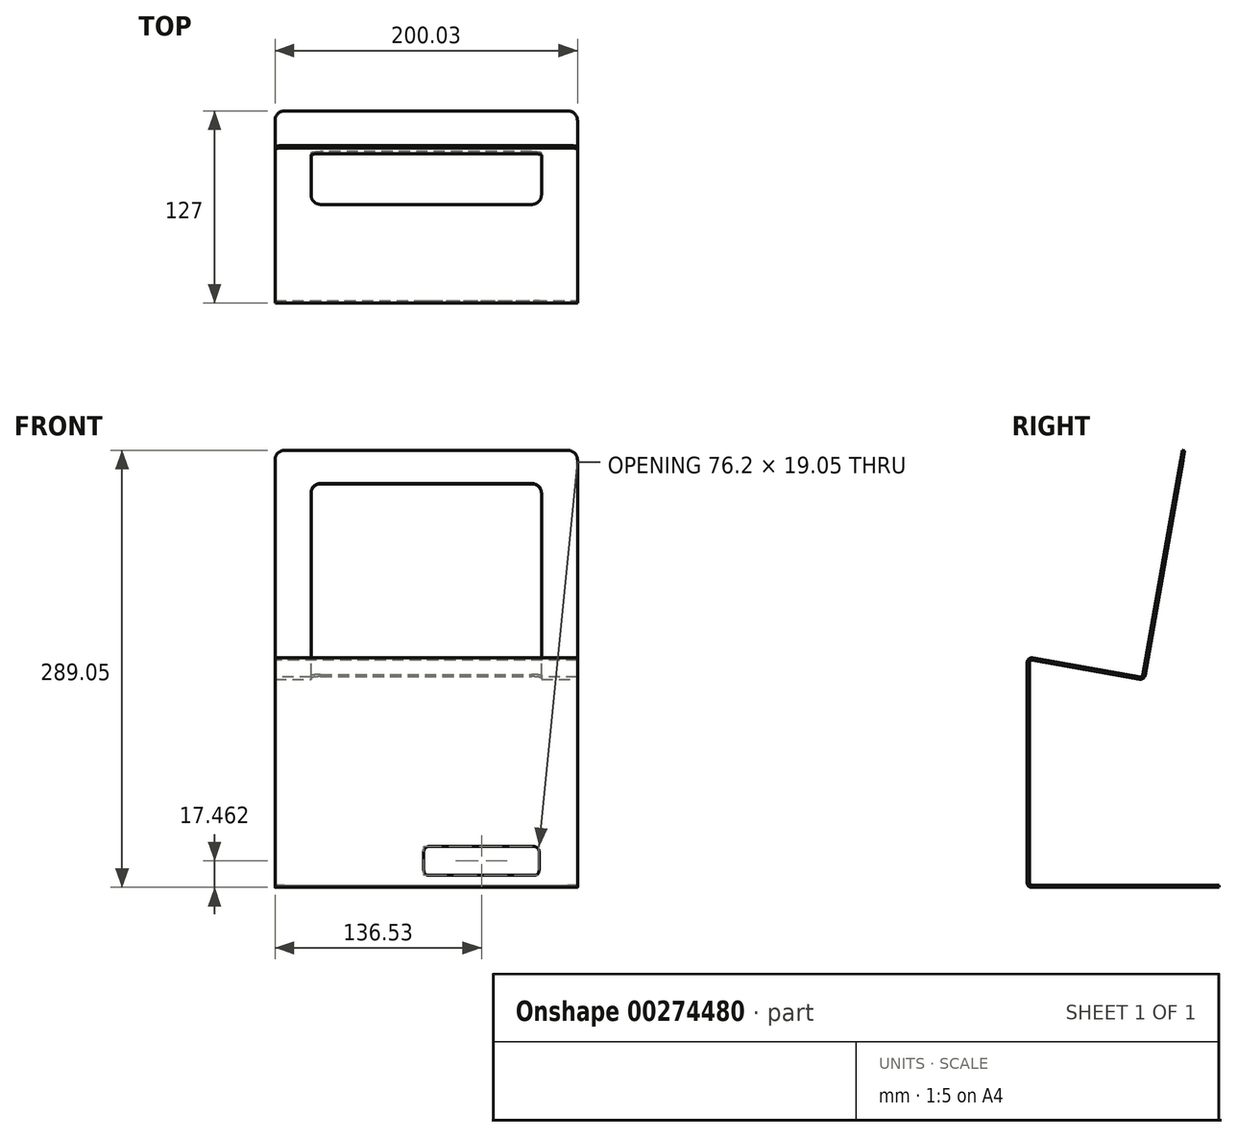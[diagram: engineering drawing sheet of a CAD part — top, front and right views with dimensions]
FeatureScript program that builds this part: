
annotation { "Feature Type Name" : "Feature", "Feature Type Description" : "" }
export const myFeature = defineFeature(function(context is Context, id is Id, definition is map)
    precondition{}
    {
        {
            var Q0;
            Q0=qCreatedBy(makeId("Right.planeOp"),FACE);
            var sketch = newSketch(context, id + "F0", { "sketchPlane" : qUnion([Q0])});
            skLineSegment(sketch, "E0", {"start": v(0, 0) * mm, "end": v(-76.2, 0) * mm});
            skLineSegment(sketch, "E1", {"start": v(-76.2, 0) * mm, "end": v(-76.2, 152.4) * mm});
            skLineSegment(sketch, "E2", {"start": v(-76.2, 152.4) * mm, "end": v(0, 138.96) * mm});
            skLineSegment(sketch, "E3", {"start": v(0, 138.96) * mm, "end": v(26.46, 289.05) * mm});
            skLineSegment(sketch, "E4.0", {"start": v(1.23, 137.2) * mm, "end": v(27.96, 288.78) * mm});
            skLineSegment(sketch, "E4.1", {"start": v(-74.68, 150.59) * mm, "end": v(1.23, 137.2) * mm});
            skLineSegment(sketch, "E4.2", {"start": v(-74.68, 1.52) * mm, "end": v(-74.68, 150.59) * mm});
            skLineSegment(sketch, "E4.3", {"start": v(0, 1.52) * mm, "end": v(-74.68, 1.52) * mm});
            skLineSegment(sketch, "E5", {"start": v(0, 1.52) * mm, "end": v(0, 0) * mm});
            skLineSegment(sketch, "E6", {"start": v(26.46, 289.05) * mm, "end": v(27.96, 288.78) * mm});
            skSolve(sketch);
        }
        {
            var Q0;
            Q0=makeQuery(id+"F0.imprint","IMPRINT",FACE,{"disambiguationData":[TD([[makeQuery(id+"F0.imprint","IMPRINT",EDGE,{"derivedFrom":sQuery(id+"F0.wireOp",EDGE,"E0")}),-1.0]])]});
            extrude(context, id + "F1", {"entities" : qUnion([Q0]), "oppositeDirection" : true, "depth" : 200.02 * mm});
        }
        {
            var Q0;
            {var subQ0=sQuery(id+"F0.wireOp",EDGE,"E3");var subQ1=sQuery(id+"F0.wireOp",EDGE,"E2");Q0=makeQuery(id+"FNieFErg1aXtviF_1.boolean.opBoolean","SPLIT",EDGE,{"disambiguationData":[TD([makeQuery(id+"FNieFErg1aXtviF_1.opExtrude","SWEPT_FACE",FACE,{"disambiguationData":[OSD([sQuery(id+"FGQBqfSR68ftS2d_1.wireOp",EDGE,"9EZzOPAj-x158-Ry3P-4ziS-DGyLsCyLf1xe.right")])]})])],"derivedFrom":makeQuery(id+"F1.opExtrude","SWEPT_EDGE",EDGE,{"disambiguationData":[OSD([subQ1,subQ0])]})});}
            var Q1;
            {var subQ0=sQuery(id+"F0.wireOp",EDGE,"E3");var subQ1=sQuery(id+"F0.wireOp",EDGE,"E2");Q1=makeQuery(id+"FNieFErg1aXtviF_1.boolean.opBoolean","SPLIT",EDGE,{"disambiguationData":[TD([makeQuery(id+"FNieFErg1aXtviF_1.opExtrude","SWEPT_FACE",FACE,{"disambiguationData":[OSD([sQuery(id+"FGQBqfSR68ftS2d_1.wireOp",EDGE,"9EZzOPAj-x158-Ry3P-4ziS-DGyLsCyLf1xe.left")])]})])],"derivedFrom":makeQuery(id+"F1.opExtrude","SWEPT_EDGE",EDGE,{"disambiguationData":[OSD([subQ1,subQ0])]})});}
            var Q2;
            Q2=makeQuery(id+"F1.opExtrude","SWEPT_EDGE",EDGE,{"disambiguationData":[OSD([sQuery(id+"F0.wireOp",EDGE,"E4.1"),sQuery(id+"F0.wireOp",EDGE,"E4.2")])]});
            var Q3;
            Q3=makeQuery(id+"F1.opExtrude","SWEPT_EDGE",EDGE,{"disambiguationData":[OSD([sQuery(id+"F0.wireOp",EDGE,"E4.2"),sQuery(id+"F0.wireOp",EDGE,"E4.3")])]});
            fillet(context, id + "F2", {"entities" : qUnion([Q0, Q1, Q2, Q3]), "radius" : 1.52 * mm, "tangentPropagation" : true, "allowEdgeOverflow" : false});
        }
        {
            var Q0;
            {var subQ0=sQuery(id+"F0.wireOp",EDGE,"E4.1");var subQ1=sQuery(id+"F0.wireOp",EDGE,"E4.0");Q0=makeQuery(id+"FNieFErg1aXtviF_1.boolean.opBoolean","SPLIT",EDGE,{"disambiguationData":[TD([makeQuery(id+"FNieFErg1aXtviF_1.opExtrude","SWEPT_FACE",FACE,{"disambiguationData":[OSD([sQuery(id+"FGQBqfSR68ftS2d_1.wireOp",EDGE,"9EZzOPAj-x158-Ry3P-4ziS-DGyLsCyLf1xe.right")])]})])],"derivedFrom":makeQuery(id+"F1.opExtrude","SWEPT_EDGE",EDGE,{"disambiguationData":[OSD([subQ1,subQ0])]})});}
            var Q1;
            {var subQ0=sQuery(id+"F0.wireOp",EDGE,"E4.1");var subQ1=sQuery(id+"F0.wireOp",EDGE,"E4.0");Q1=makeQuery(id+"FNieFErg1aXtviF_1.boolean.opBoolean","SPLIT",EDGE,{"disambiguationData":[TD([makeQuery(id+"FNieFErg1aXtviF_1.opExtrude","SWEPT_FACE",FACE,{"disambiguationData":[OSD([sQuery(id+"FGQBqfSR68ftS2d_1.wireOp",EDGE,"9EZzOPAj-x158-Ry3P-4ziS-DGyLsCyLf1xe.left")])]})])],"derivedFrom":makeQuery(id+"F1.opExtrude","SWEPT_EDGE",EDGE,{"disambiguationData":[OSD([subQ1,subQ0])]})});}
            var Q2;
            Q2=makeQuery(id+"F1.opExtrude","SWEPT_EDGE",EDGE,{"disambiguationData":[OSD([sQuery(id+"F0.wireOp",EDGE,"E1"),sQuery(id+"F0.wireOp",EDGE,"E2")])]});
            var Q3;
            Q3=makeQuery(id+"F1.opExtrude","SWEPT_EDGE",EDGE,{"disambiguationData":[OSD([sQuery(id+"F0.wireOp",EDGE,"E0"),sQuery(id+"F0.wireOp",EDGE,"E1")])]});
            fillet(context, id + "F3", {"entities" : qUnion([Q0, Q1, Q2, Q3]), "radius" : 3.04 * mm, "tangentPropagation" : true, "allowEdgeOverflow" : false});
        }
        {
            var Q0;
            Q0=makeQuery(id+"F1.opExtrude","SWEPT_FACE",FACE,{"disambiguationData":[OSD([sQuery(id+"F0.wireOp",EDGE,"E5")])]});
            extrude(context, id + "F4", {"entities" : qUnion([Q0]), "operationType" : NewBodyOperationType.ADD, "depth" : 50.8 * mm});
        }
        {
            var Q0;
            Q0=makeQuery(id+"F1.opExtrude","SWEPT_FACE",FACE,{"disambiguationData":[OSD([sQuery(id+"F0.wireOp",EDGE,"E1")])]});
            var sketch = newSketch(context, id + "F5", { "sketchPlane" : qUnion([Q0])});
            skLineSegment(sketch, "E7.bottom", {"start": v(-25.4, 7.94) * mm, "end": v(-101.6, 7.94) * mm});
            skLineSegment(sketch, "E7.top", {"start": v(-25.4, 26.99) * mm, "end": v(-101.6, 26.99) * mm});
            skLineSegment(sketch, "E7.left", {"start": v(-25.4, 7.94) * mm, "end": v(-25.4, 26.99) * mm});
            skLineSegment(sketch, "E7.right", {"start": v(-101.6, 7.94) * mm, "end": v(-101.6, 26.99) * mm});
            skSolve(sketch);
        }
        {
            var Q0;
            Q0=makeQuery(id+"F5.imprint","IMPRINT",FACE,{"disambiguationData":[TD([[makeQuery(id+"F5.imprint","IMPRINT",EDGE,{"derivedFrom":sQuery(id+"F5.wireOp",EDGE,"E7.bottom")}),-1.0]])]});
            extrude(context, id + "F6", {"entities" : qUnion([Q0]), "operationType" : NewBodyOperationType.REMOVE, "oppositeDirection" : true, "depth" : 25.4 * mm});
        }
        {
            var Q0;
            Q0=makeQuery(id+"F1.opExtrude","SWEPT_FACE",FACE,{"disambiguationData":[OSD([sQuery(id+"F0.wireOp",EDGE,"E4.0")])]});
            var sketch = newSketch(context, id + "F7", { "sketchPlane" : qUnion([Q0])});
            skLineSegment(sketch, "E8", {"start": v(23.81, 128.98) * mm, "end": v(176.21, 128.98) * mm});
            skLineSegment(sketch, "E9", {"start": v(100.01, 128.98) * mm, "end": v(100.01, 100.27) * mm, "construction": true});
            skLineSegment(sketch, "E10", {"start": v(23.81, 128.98) * mm, "end": v(23.81, 267.03) * mm});
            skLineSegment(sketch, "E11", {"start": v(176.21, 128.98) * mm, "end": v(176.21, 267.03) * mm});
            skLineSegment(sketch, "E12", {"start": v(23.81, 267.03) * mm, "end": v(176.21, 267.03) * mm});
            skSolve(sketch);
        }
        {
            var Q0;
            Q0 = qSketchRegion(id + "F7", true);
            extrude(context, id + "F8", {"entities" : qUnion([Q0]), "operationType" : NewBodyOperationType.REMOVE, "oppositeDirection" : true, "depth" : 12.7 * mm});
        }
        {
            var Q0;
            Q0=makeQuery(id+"F1.opExtrude","CAP_EDGE",EDGE,{"disambiguationData":[OSD([sQuery(id+"F0.wireOp",EDGE,"E6")])],"isStart":true});
            var Q1;
            {var subQ0=sQuery(id+"F0.wireOp",EDGE,"E5");Q1=makeQuery(id+"F4.opExtrude","CAP_EDGE",EDGE,{"disambiguationData":[OSD([subQ0]),TDD([makeQuery(id+"F1.opExtrude","CAP_EDGE",EDGE,{"disambiguationData":[OSD([subQ0])],"isStart":true})])],"isStart":false});}
            var Q2;
            Q2=makeQuery(id+"F1.opExtrude","CAP_EDGE",EDGE,{"disambiguationData":[OSD([sQuery(id+"F0.wireOp",EDGE,"E6")])],"isStart":false});
            var Q3;
            {var subQ0=sQuery(id+"F0.wireOp",EDGE,"E5");Q3=makeQuery(id+"F4.opExtrude","CAP_EDGE",EDGE,{"disambiguationData":[OSD([subQ0]),TDD([makeQuery(id+"F1.opExtrude","CAP_EDGE",EDGE,{"disambiguationData":[OSD([subQ0])],"isStart":false})])],"isStart":false});}
            var Q4;
            Q4=makeQuery(id+"F8.boolean.opBoolean","COPY",EDGE,{"derivedFrom":makeQuery(id+"F8.opExtrude","SWEPT_EDGE",EDGE,{"disambiguationData":[OSD([sQuery(id+"F7.wireOp",EDGE,"E11"),sQuery(id+"F7.wireOp",EDGE,"E12")])]})});
            var Q5;
            Q5=makeQuery(id+"F8.boolean.opBoolean","COPY",EDGE,{"derivedFrom":makeQuery(id+"F8.opExtrude","SWEPT_EDGE",EDGE,{"disambiguationData":[OSD([sQuery(id+"F7.wireOp",EDGE,"E10"),sQuery(id+"F7.wireOp",EDGE,"E12")])]})});
            var Q6;
            Q6=makeQuery(id+"F8.boolean.opBoolean","COPY",EDGE,{"derivedFrom":makeQuery(id+"F8.opExtrude","CAP_EDGE",EDGE,{"disambiguationData":[OSD([sQuery(id+"F7.wireOp",EDGE,"E11")])],"isStart":false})});
            var Q7;
            Q7=makeQuery(id+"F8.boolean.opBoolean","COPY",EDGE,{"derivedFrom":makeQuery(id+"F8.opExtrude","CAP_EDGE",EDGE,{"disambiguationData":[OSD([sQuery(id+"F7.wireOp",EDGE,"E10")])],"isStart":false})});
            fillet(context, id + "F9", {"entities" : qUnion([Q0, Q1, Q2, Q3, Q4, Q5, Q6, Q7]), "radius" : 6.35 * mm, "tangentPropagation" : true, "allowEdgeOverflow" : false});
        }
        {
            var Q0;
            Q0=makeQuery(id+"F6.boolean.opBoolean","COPY",EDGE,{"derivedFrom":makeQuery(id+"F6.opExtrude","SWEPT_EDGE",EDGE,{"disambiguationData":[OSD([sQuery(id+"F5.wireOp",EDGE,"E7.top"),sQuery(id+"F5.wireOp",EDGE,"E7.right")])]})});
            var Q1;
            Q1=makeQuery(id+"F6.boolean.opBoolean","COPY",EDGE,{"derivedFrom":makeQuery(id+"F6.opExtrude","SWEPT_EDGE",EDGE,{"disambiguationData":[OSD([sQuery(id+"F5.wireOp",EDGE,"E7.top"),sQuery(id+"F5.wireOp",EDGE,"E7.left")])]})});
            var Q2;
            Q2=makeQuery(id+"F6.boolean.opBoolean","COPY",EDGE,{"derivedFrom":makeQuery(id+"F6.opExtrude","SWEPT_EDGE",EDGE,{"disambiguationData":[OSD([sQuery(id+"F5.wireOp",EDGE,"E7.bottom"),sQuery(id+"F5.wireOp",EDGE,"E7.left")])]})});
            var Q3;
            Q3=makeQuery(id+"F6.boolean.opBoolean","COPY",EDGE,{"derivedFrom":makeQuery(id+"F6.opExtrude","SWEPT_EDGE",EDGE,{"disambiguationData":[OSD([sQuery(id+"F5.wireOp",EDGE,"E7.bottom"),sQuery(id+"F5.wireOp",EDGE,"E7.right")])]})});
            fillet(context, id + "F10", {"entities" : qUnion([Q0, Q1, Q2, Q3]), "radius" : 3.17 * mm, "tangentPropagation" : true, "allowEdgeOverflow" : false});
        }
    });
